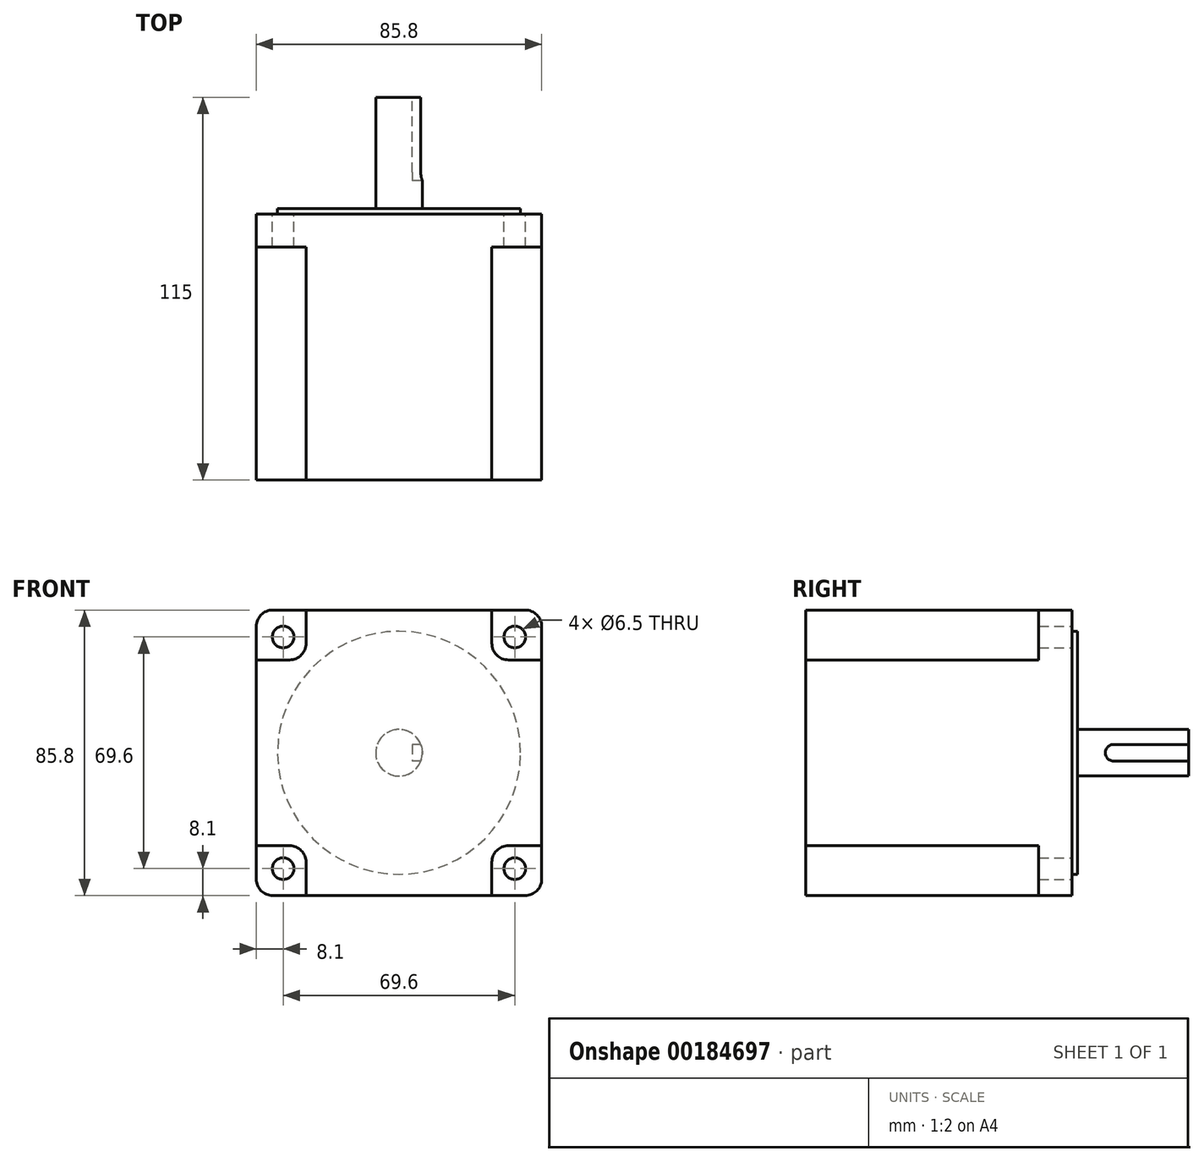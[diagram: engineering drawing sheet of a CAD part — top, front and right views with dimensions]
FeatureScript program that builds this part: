
annotation { "Feature Type Name" : "Feature", "Feature Type Description" : "" }
export const myFeature = defineFeature(function(context is Context, id is Id, definition is map)
    precondition{}
    {
        {
            var Q0;
            Q0=qCreatedBy(makeId("Front.planeOp"),FACE);
            var sketch = newSketch(context, id + "F0", { "sketchPlane" : qUnion([Q0])});
            skLineSegment(sketch, "E0.bottom", {"start": v(-37.9, 42.9) * mm, "end": v(37.9, 42.9) * mm});
            skLineSegment(sketch, "E0.top", {"start": v(-37.9, -42.9) * mm, "end": v(37.9, -42.9) * mm});
            skLineSegment(sketch, "E0.left", {"start": v(-42.9, 37.9) * mm, "end": v(-42.9, -37.9) * mm});
            skLineSegment(sketch, "E0.right", {"start": v(42.9, 37.9) * mm, "end": v(42.9, -37.9) * mm});
            skArc(sketch, "E1.filletArc", {"start": v(-42.9, -37.9) * mm, "mid": v(-41.44, -41.44) * mm, "end": v(-37.9, -42.9) * mm});
            skPoint(sketch, "E2.visualSharp", {"position": v(-42.9, 42.9) * mm});
            skArc(sketch, "E2.filletArc", {"start": v(-37.9, 42.9) * mm, "mid": v(-41.44, 41.44) * mm, "end": v(-42.9, 37.9) * mm});
            skPoint(sketch, "E3.visualSharp", {"position": v(42.9, 42.9) * mm});
            skArc(sketch, "E3.filletArc", {"start": v(42.9, 37.9) * mm, "mid": v(41.44, 41.44) * mm, "end": v(37.9, 42.9) * mm});
            skPoint(sketch, "E4.visualSharp", {"position": v(42.9, -42.9) * mm});
            skArc(sketch, "E4.filletArc", {"start": v(37.9, -42.9) * mm, "mid": v(41.44, -41.44) * mm, "end": v(42.9, -37.9) * mm});
            skSolve(sketch);
        }
        {
            var Q0;
            Q0=makeQuery(id+"F0.imprint","IMPRINT",FACE,{"disambiguationData":[TD([[makeQuery(id+"F0.imprint","IMPRINT",EDGE,{"derivedFrom":sQuery(id+"F0.wireOp",EDGE,"E0.bottom")}),-1.0]])]});
            extrude(context, id + "F1", {"entities" : qUnion([Q0]), "depth" : 80 * mm});
        }
        {
            var Q0;
            Q0=makeQuery(id+"F1.opExtrude","CAP_FACE",FACE,{"disambiguationData":[OSD([sQuery(id+"F0.wireOp",EDGE,"E0.bottom"),sQuery(id+"F0.wireOp",EDGE,"E0.top"),sQuery(id+"F0.wireOp",EDGE,"E0.left"),sQuery(id+"F0.wireOp",EDGE,"E0.right"),sQuery(id+"F0.wireOp",EDGE,"E1.filletArc"),sQuery(id+"F0.wireOp",EDGE,"E2.filletArc"),sQuery(id+"F0.wireOp",EDGE,"E3.filletArc"),sQuery(id+"F0.wireOp",EDGE,"E4.filletArc")])],"isStart":false});
            var sketch = newSketch(context, id + "F2", { "sketchPlane" : qUnion([Q0])});
            skLineSegment(sketch, "E5.bottom", {"start": v(27.9, 42.9) * mm, "end": v(42.9, 42.9) * mm});
            skLineSegment(sketch, "E5.top", {"start": v(27.9, 27.9) * mm, "end": v(42.9, 27.9) * mm});
            skLineSegment(sketch, "E5.left", {"start": v(27.9, 42.9) * mm, "end": v(27.9, 27.9) * mm});
            skLineSegment(sketch, "E5.right", {"start": v(42.9, 42.9) * mm, "end": v(42.9, 27.9) * mm});
            skLineSegment(sketch, "E6.MirrorCS", {"start": v(-27.9, 42.9) * mm, "end": v(-42.9, 42.9) * mm});
            skLineSegment(sketch, "E7.MirrorCS", {"start": v(-27.9, 27.9) * mm, "end": v(-42.9, 27.9) * mm});
            skLineSegment(sketch, "E8.MirrorCS", {"start": v(-42.9, 42.9) * mm, "end": v(-42.9, 27.9) * mm});
            skLineSegment(sketch, "E9.MirrorCS", {"start": v(-27.9, 42.9) * mm, "end": v(-27.9, 27.9) * mm});
            skLineSegment(sketch, "E10.MirrorCS", {"start": v(-27.9, -42.9) * mm, "end": v(-27.9, -27.9) * mm});
            skLineSegment(sketch, "E11.MirrorCS", {"start": v(-27.9, -42.9) * mm, "end": v(-42.9, -42.9) * mm});
            skLineSegment(sketch, "E12.MirrorCS", {"start": v(-27.9, -27.9) * mm, "end": v(-42.9, -27.9) * mm});
            skLineSegment(sketch, "E13.MirrorCS", {"start": v(-42.9, -42.9) * mm, "end": v(-42.9, -27.9) * mm});
            skLineSegment(sketch, "E14.MirrorCS", {"start": v(42.9, -42.9) * mm, "end": v(42.9, -27.9) * mm});
            skLineSegment(sketch, "E15.MirrorCS", {"start": v(27.9, -27.9) * mm, "end": v(42.9, -27.9) * mm});
            skLineSegment(sketch, "E16.MirrorCS", {"start": v(27.9, -42.9) * mm, "end": v(42.9, -42.9) * mm});
            skLineSegment(sketch, "E17.MirrorCS", {"start": v(27.9, -42.9) * mm, "end": v(27.9, -27.9) * mm});
            skSolve(sketch);
        }
        {
            var Q0;
            Q0 = qSketchRegion(id + "F2", true);
            var Q1;
            Q1=makeQuery(id+"F1.opExtrude","CAP_FACE",FACE,{"disambiguationData":[OSD([sQuery(id+"F0.wireOp",EDGE,"E0.bottom"),sQuery(id+"F0.wireOp",EDGE,"E0.top"),sQuery(id+"F0.wireOp",EDGE,"E0.left"),sQuery(id+"F0.wireOp",EDGE,"E0.right"),sQuery(id+"F0.wireOp",EDGE,"E1.filletArc"),sQuery(id+"F0.wireOp",EDGE,"E2.filletArc"),sQuery(id+"F0.wireOp",EDGE,"E3.filletArc"),sQuery(id+"F0.wireOp",EDGE,"E4.filletArc")])],"isStart":false});
            extrude(context, id + "F3", {"entities" : qUnion([Q0]), "operationType" : NewBodyOperationType.REMOVE, "oppositeDirection" : true, "endBoundEntityFace" : qUnion([Q1]), "depth" : 70 * mm});
        }
        {
            var Q0;
            Q0=makeQuery(id+"F1.opExtrude","CAP_FACE",FACE,{"disambiguationData":[OSD([sQuery(id+"F0.wireOp",EDGE,"E0.bottom"),sQuery(id+"F0.wireOp",EDGE,"E0.top"),sQuery(id+"F0.wireOp",EDGE,"E0.left"),sQuery(id+"F0.wireOp",EDGE,"E0.right"),sQuery(id+"F0.wireOp",EDGE,"E1.filletArc"),sQuery(id+"F0.wireOp",EDGE,"E2.filletArc"),sQuery(id+"F0.wireOp",EDGE,"E3.filletArc"),sQuery(id+"F0.wireOp",EDGE,"E4.filletArc")])],"isStart":true});
            var sketch = newSketch(context, id + "F4", { "sketchPlane" : qUnion([Q0])});
            skCircle(sketch, "E18", {"center": v(34.8, 34.8) * mm, "radius": 3.25 * mm});
            skCircle(sketch, "E19.MirrorC", {"center": v(-34.8, 34.8) * mm, "radius": 3.25 * mm});
            skCircle(sketch, "E20.MirrorC", {"center": v(34.8, -34.8) * mm, "radius": 3.25 * mm});
            skCircle(sketch, "E21.MirrorC", {"center": v(-34.8, -34.8) * mm, "radius": 3.25 * mm});
            skSolve(sketch);
        }
        {
            var Q0;
            Q0 = qSketchRegion(id + "F4", true);
            extrude(context, id + "F5", {"entities" : qUnion([Q0]), "operationType" : NewBodyOperationType.REMOVE, "endBound" : BoundingType.UP_TO_NEXT, "oppositeDirection" : true, "depth" : 25 * mm});
        }
        {
            var Q0;
            Q0=makeQuery(id+"F3.boolean.opBoolean","COPY",EDGE,{"derivedFrom":makeQuery(id+"F3.opExtrude","SWEPT_EDGE",EDGE,{"disambiguationData":[OSD([sQuery(id+"F0.wireOp",EDGE,"E0.left"),sQuery(id+"F2.wireOp",EDGE,"E8.MirrorCS"),sQuery(id+"F2.wireOp",EDGE,"E7.MirrorCS")])]})});
            var Q1;
            Q1=makeQuery(id+"F3.boolean.opBoolean","COPY",EDGE,{"derivedFrom":makeQuery(id+"F3.opExtrude","SWEPT_EDGE",EDGE,{"disambiguationData":[OSD([sQuery(id+"F0.wireOp",EDGE,"E0.left"),sQuery(id+"F2.wireOp",EDGE,"E13.MirrorCS"),sQuery(id+"F2.wireOp",EDGE,"E12.MirrorCS")])]})});
            var Q2;
            Q2=makeQuery(id+"F3.boolean.opBoolean","COPY",EDGE,{"derivedFrom":makeQuery(id+"F3.opExtrude","SWEPT_EDGE",EDGE,{"disambiguationData":[OSD([sQuery(id+"F2.wireOp",EDGE,"E12.MirrorCS"),sQuery(id+"F2.wireOp",EDGE,"E10.MirrorCS")])]})});
            var Q3;
            Q3=makeQuery(id+"F3.boolean.opBoolean","COPY",EDGE,{"derivedFrom":makeQuery(id+"F3.opExtrude","SWEPT_EDGE",EDGE,{"disambiguationData":[OSD([sQuery(id+"F0.wireOp",EDGE,"E0.top"),sQuery(id+"F2.wireOp",EDGE,"E10.MirrorCS"),sQuery(id+"F2.wireOp",EDGE,"E11.MirrorCS")])]})});
            var Q4;
            Q4=makeQuery(id+"F3.boolean.opBoolean","COPY",EDGE,{"derivedFrom":makeQuery(id+"F3.opExtrude","SWEPT_EDGE",EDGE,{"disambiguationData":[OSD([sQuery(id+"F0.wireOp",EDGE,"E0.top"),sQuery(id+"F2.wireOp",EDGE,"E17.MirrorCS"),sQuery(id+"F2.wireOp",EDGE,"E16.MirrorCS")])]})});
            var Q5;
            Q5=makeQuery(id+"F3.boolean.opBoolean","COPY",EDGE,{"derivedFrom":makeQuery(id+"F3.opExtrude","SWEPT_EDGE",EDGE,{"disambiguationData":[OSD([sQuery(id+"F0.wireOp",EDGE,"E0.bottom"),sQuery(id+"F2.wireOp",EDGE,"E9.MirrorCS"),sQuery(id+"F2.wireOp",EDGE,"E6.MirrorCS")])]})});
            var Q6;
            Q6=makeQuery(id+"F3.boolean.opBoolean","COPY",EDGE,{"derivedFrom":makeQuery(id+"F3.opExtrude","SWEPT_EDGE",EDGE,{"disambiguationData":[OSD([sQuery(id+"F2.wireOp",EDGE,"E17.MirrorCS"),sQuery(id+"F2.wireOp",EDGE,"E15.MirrorCS")])]})});
            var Q7;
            Q7=makeQuery(id+"F3.boolean.opBoolean","COPY",EDGE,{"derivedFrom":makeQuery(id+"F3.opExtrude","SWEPT_EDGE",EDGE,{"disambiguationData":[OSD([sQuery(id+"F0.wireOp",EDGE,"E0.right"),sQuery(id+"F2.wireOp",EDGE,"E14.MirrorCS"),sQuery(id+"F2.wireOp",EDGE,"E15.MirrorCS")])]})});
            var Q8;
            Q8=makeQuery(id+"F3.boolean.opBoolean","COPY",EDGE,{"derivedFrom":makeQuery(id+"F3.opExtrude","SWEPT_EDGE",EDGE,{"disambiguationData":[OSD([sQuery(id+"F0.wireOp",EDGE,"E0.right"),sQuery(id+"F2.wireOp",EDGE,"E5.right"),sQuery(id+"F2.wireOp",EDGE,"E5.top")])]})});
            var Q9;
            Q9=makeQuery(id+"F3.boolean.opBoolean","COPY",EDGE,{"derivedFrom":makeQuery(id+"F3.opExtrude","SWEPT_EDGE",EDGE,{"disambiguationData":[OSD([sQuery(id+"F0.wireOp",EDGE,"E0.bottom"),sQuery(id+"F2.wireOp",EDGE,"E5.bottom"),sQuery(id+"F2.wireOp",EDGE,"E5.left")])]})});
            var Q10;
            Q10=makeQuery(id+"F3.boolean.opBoolean","COPY",EDGE,{"derivedFrom":makeQuery(id+"F3.opExtrude","SWEPT_EDGE",EDGE,{"disambiguationData":[OSD([sQuery(id+"F2.wireOp",EDGE,"E5.top"),sQuery(id+"F2.wireOp",EDGE,"E5.left")])]})});
            var Q11;
            Q11=makeQuery(id+"F3.boolean.opBoolean","COPY",EDGE,{"derivedFrom":makeQuery(id+"F3.opExtrude","SWEPT_EDGE",EDGE,{"disambiguationData":[OSD([sQuery(id+"F2.wireOp",EDGE,"E9.MirrorCS"),sQuery(id+"F2.wireOp",EDGE,"E7.MirrorCS")])]})});
            fillet(context, id + "F6", {"entities" : qUnion([Q0, Q1, Q2, Q3, Q4, Q5, Q6, Q7, Q8, Q9, Q10, Q11]), "radius" : 5 * mm, "tangentPropagation" : true, "allowEdgeOverflow" : false});
        }
        {
            var Q0;
            Q0=makeQuery(id+"F1.opExtrude","CAP_FACE",FACE,{"disambiguationData":[OSD([sQuery(id+"F0.wireOp",EDGE,"E0.bottom"),sQuery(id+"F0.wireOp",EDGE,"E0.top"),sQuery(id+"F0.wireOp",EDGE,"E0.left"),sQuery(id+"F0.wireOp",EDGE,"E0.right"),sQuery(id+"F0.wireOp",EDGE,"E1.filletArc"),sQuery(id+"F0.wireOp",EDGE,"E2.filletArc"),sQuery(id+"F0.wireOp",EDGE,"E3.filletArc"),sQuery(id+"F0.wireOp",EDGE,"E4.filletArc")])],"isStart":true});
            var sketch = newSketch(context, id + "F7", { "sketchPlane" : qUnion([Q0])});
            skCircle(sketch, "E22", {"center": v(0, 0) * mm, "radius": 36.5 * mm});
            skSolve(sketch);
        }
        {
            var Q0;
            Q0 = qSketchRegion(id + "F7", true);
            extrude(context, id + "F8", {"entities" : qUnion([Q0]), "operationType" : NewBodyOperationType.ADD, "depth" : 1.6 * mm});
        }
        {
            var Q0;
            Q0=makeQuery(id+"F1.opExtrude","CAP_FACE",FACE,{"disambiguationData":[OSD([sQuery(id+"F0.wireOp",EDGE,"E0.bottom"),sQuery(id+"F0.wireOp",EDGE,"E0.top"),sQuery(id+"F0.wireOp",EDGE,"E0.left"),sQuery(id+"F0.wireOp",EDGE,"E0.right"),sQuery(id+"F0.wireOp",EDGE,"E1.filletArc"),sQuery(id+"F0.wireOp",EDGE,"E2.filletArc"),sQuery(id+"F0.wireOp",EDGE,"E3.filletArc"),sQuery(id+"F0.wireOp",EDGE,"E4.filletArc")])],"isStart":true});
            var sketch = newSketch(context, id + "F9", { "sketchPlane" : qUnion([Q0])});
            skCircle(sketch, "E23", {"center": v(0, 0) * mm, "radius": 7 * mm});
            skSolve(sketch);
        }
        {
            var Q0;
            Q0 = qSketchRegion(id + "F9", true);
            var Q1;
            Q1=sQuery(id+"F9.wireOp",EDGE,"E23");
            extrude(context, id + "F10", {"entities" : qUnion([Q0]), "operationType" : NewBodyOperationType.ADD, "surfaceEntities" : qUnion([Q1]), "depth" : 35 * mm});
        }
        {
            var Q0;
            Q0=qCreatedBy(makeId("Right.planeOp"),FACE);
            cPlane(context, id + "F11", {"entities" : qUnion([Q0]), "cplaneType" : CPlaneType.OFFSET, "offset" : 4 * mm, "width" : 150 * mm, "height" : 150 * mm});
        }
        {
            var Q0;
            Q0=qCreatedBy(id+"F11.planeOp",FACE);
            var sketch = newSketch(context, id + "F12", { "sketchPlane" : qUnion([Q0])});
            skLineSegment(sketch, "E24.top", {"start": v(12.5, 2.5) * mm, "end": v(35, 2.5) * mm});
            skLineSegment(sketch, "E24.left", {"start": v(10, 0) * mm, "end": v(10, 0) * mm});
            skLineSegment(sketch, "E24.right", {"start": v(35, 0) * mm, "end": v(35, 2.5) * mm});
            skPoint(sketch, "E25.visualSharp", {"position": v(10, 2.5) * mm});
            skArc(sketch, "E25.filletArc", {"start": v(12.5, 2.5) * mm, "mid": v(10.73, 1.77) * mm, "end": v(10, 0) * mm});
            skArc(sketch, "E26.MirrorCS", {"start": v(12.5, -2.5) * mm, "mid": v(10.73, -1.77) * mm, "end": v(10, 0) * mm});
            skLineSegment(sketch, "E27.MirrorCS", {"start": v(35, 0) * mm, "end": v(35, -2.5) * mm});
            skLineSegment(sketch, "E28.MirrorCS", {"start": v(12.5, -2.5) * mm, "end": v(35, -2.5) * mm});
            skPoint(sketch, "E29.MirrorP", {"position": v(10, -2.5) * mm});
            skSolve(sketch);
        }
        {
            var Q0;
            Q0 = qSketchRegion(id + "F12", true);
            extrude(context, id + "F13", {"entities" : qUnion([Q0]), "operationType" : NewBodyOperationType.REMOVE, "depth" : 5 * mm});
        }
    });
